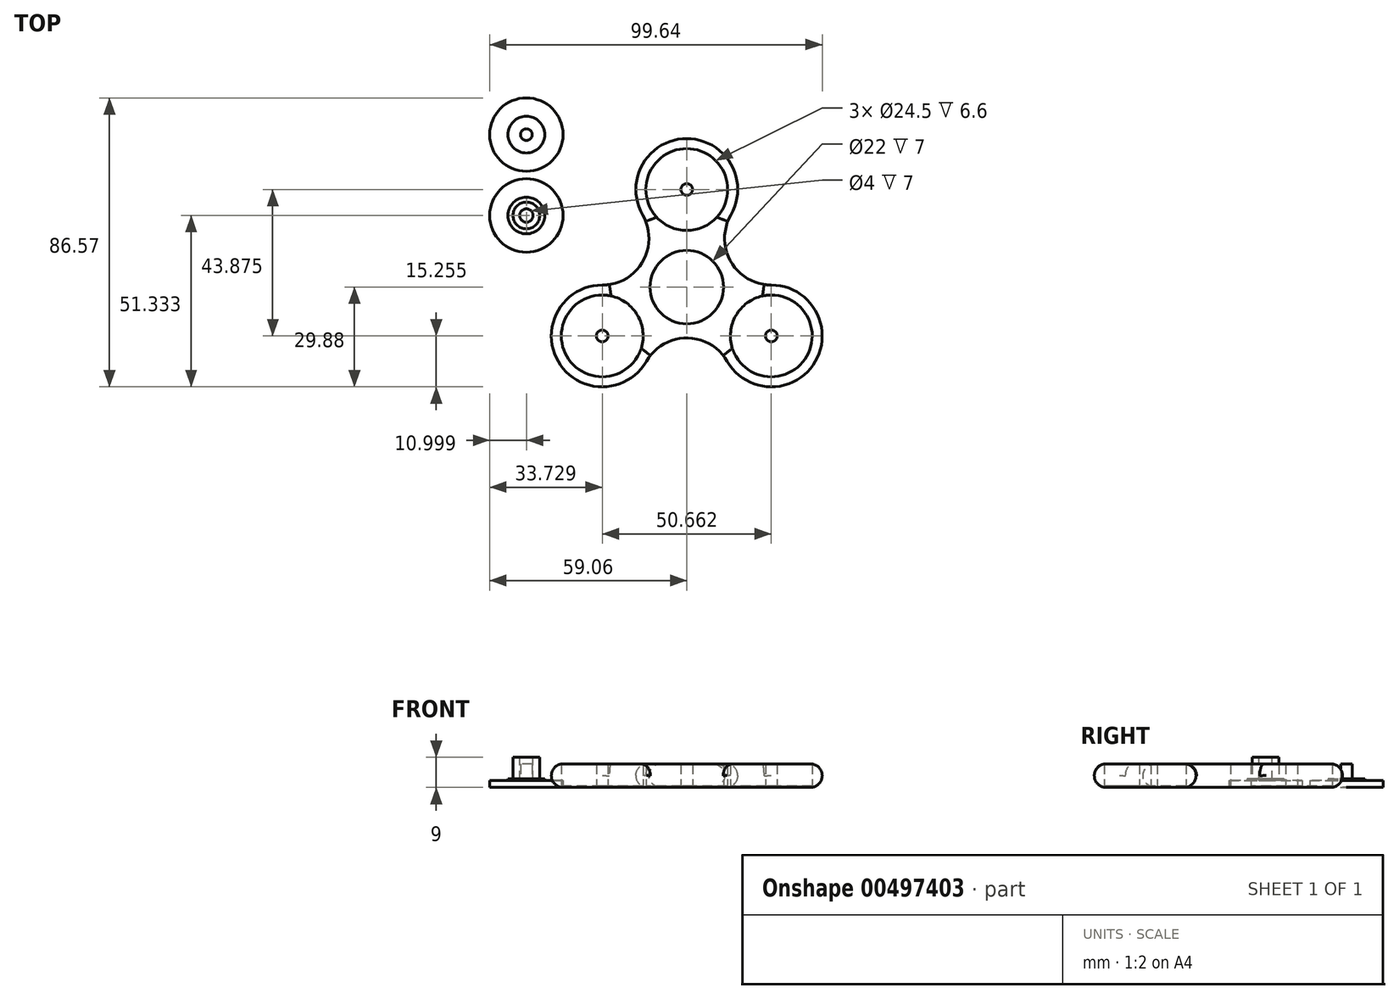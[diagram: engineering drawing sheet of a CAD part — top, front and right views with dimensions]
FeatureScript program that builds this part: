
annotation { "Feature Type Name" : "Feature", "Feature Type Description" : "" }
export const myFeature = defineFeature(function(context is Context, id is Id, definition is map)
    precondition{}
    {
        {
            var Q0;
            Q0=qCreatedBy(makeId("Top.planeOp"),FACE);
            var sketch = newSketch(context, id + "F0", { "sketchPlane" : qUnion([Q0])});
            skCircle(sketch, "E0", {"center": v(0, 0) * mm, "radius": 11 * mm});
            skCircle(sketch, "E1", {"center": v(0, 0) * mm, "radius": 14 * mm});
            skCircle(sketch, "E2", {"center": v(0, 29.25) * mm, "radius": 12.25 * mm});
            skCircle(sketch, "E3", {"center": v(0, 29.25) * mm, "radius": 1.75 * mm});
            skCircle(sketch, "E4", {"center": v(0, 29.25) * mm, "radius": 15.25 * mm});
            skCircle(sketch, "E5.1.0", {"center": v(-25.33, -14.62) * mm, "radius": 15.25 * mm});
            skCircle(sketch, "E5.1.1", {"center": v(-25.33, -14.62) * mm, "radius": 1.75 * mm});
            skCircle(sketch, "E5.1.2", {"center": v(-25.33, -14.62) * mm, "radius": 12.25 * mm});
            skCircle(sketch, "E5.2.0", {"center": v(25.33, -14.62) * mm, "radius": 15.25 * mm});
            skCircle(sketch, "E5.2.1", {"center": v(25.33, -14.62) * mm, "radius": 1.75 * mm});
            skCircle(sketch, "E5.2.2", {"center": v(25.33, -14.62) * mm, "radius": 12.25 * mm});
            skArc(sketch, "E6", {"start": v(-25.33, 0.63) * mm, "mid": v(-13.2, 7.62) * mm, "end": v(-13.2, 21.62) * mm});
            skArc(sketch, "E7.1.0", {"start": v(12.12, -22.25) * mm, "mid": v(0, -15.25) * mm, "end": v(-12.12, -22.25) * mm});
            skArc(sketch, "E7.2.0", {"start": v(13.2, 21.63) * mm, "mid": v(13.2, 7.63) * mm, "end": v(25.33, 0.63) * mm});
            skSolve(sketch);
        }
        {
            var Q0;
            Q0=makeQuery(id+"F0.imprint","IMPRINT",FACE,{"disambiguationData":[TD([[makeQuery(id+"F0.imprint","IMPRINT",EDGE,{"derivedFrom":sQuery(id+"F0.wireOp",EDGE,"E2")}),-1.0]])]});
            var Q1;
            {var subQ5=sQuery(id+"F0.wireOp",EDGE,"E6");Q1=makeQuery(id+"F0.imprint","IMPRINT",FACE,{"disambiguationData":[TD([[makeQuery(id+"F0.imprint","IMPRINT",EDGE,{"derivedFrom":subQ5}),-1.0]])]});}
            var Q2;
            Q2=makeQuery(id+"F0.imprint","IMPRINT",FACE,{"disambiguationData":[TD([[makeQuery(id+"F0.imprint","IMPRINT",EDGE,{"derivedFrom":sQuery(id+"F0.wireOp",EDGE,"E0")}),-1.0]])]});
            var Q3;
            {var subQ5=sQuery(id+"F0.wireOp",EDGE,"E7.2.0");Q3=makeQuery(id+"F0.imprint","IMPRINT",FACE,{"disambiguationData":[TD([[makeQuery(id+"F0.imprint","IMPRINT",EDGE,{"derivedFrom":subQ5}),-1.0]])]});}
            var Q4;
            Q4=makeQuery(id+"F0.imprint","IMPRINT",FACE,{"disambiguationData":[TD([[makeQuery(id+"F0.imprint","IMPRINT",EDGE,{"derivedFrom":sQuery(id+"F0.wireOp",EDGE,"E5.2.2")}),-1.0]])]});
            var Q5;
            {var subQ5=sQuery(id+"F0.wireOp",EDGE,"E7.1.0");Q5=makeQuery(id+"F0.imprint","IMPRINT",FACE,{"disambiguationData":[TD([[makeQuery(id+"F0.imprint","IMPRINT",EDGE,{"derivedFrom":subQ5}),-1.0]])]});}
            var Q6;
            Q6=makeQuery(id+"F0.imprint","IMPRINT",FACE,{"disambiguationData":[TD([[makeQuery(id+"F0.imprint","IMPRINT",EDGE,{"derivedFrom":sQuery(id+"F0.wireOp",EDGE,"E5.1.2")}),-1.0]])]});
            extrude(context, id + "F1", {"entities" : qUnion([Q0, Q1, Q2, Q3, Q4, Q5, Q6]), "depth" : 7 * mm});
        }
        {
            var Q0;
            Q0=makeQuery(id+"F0.imprint","IMPRINT",FACE,{"disambiguationData":[TD([[makeQuery(id+"F0.imprint","IMPRINT",EDGE,{"derivedFrom":sQuery(id+"F0.wireOp",EDGE,"E2")}),1.0]])]});
            var Q1;
            Q1=makeQuery(id+"F0.imprint","IMPRINT",FACE,{"disambiguationData":[TD([[makeQuery(id+"F0.imprint","IMPRINT",EDGE,{"derivedFrom":sQuery(id+"F0.wireOp",EDGE,"E5.1.1")}),-1.0]])]});
            var Q2;
            Q2=makeQuery(id+"F0.imprint","IMPRINT",FACE,{"disambiguationData":[TD([[makeQuery(id+"F0.imprint","IMPRINT",EDGE,{"derivedFrom":sQuery(id+"F0.wireOp",EDGE,"E5.2.1")}),-1.0]])]});
            extrude(context, id + "F2", {"entities" : qUnion([Q0, Q1, Q2]), "operationType" : NewBodyOperationType.ADD, "depth" : 0.4 * mm});
        }
        {
            var Q0;
            Q0=makeQuery(id+"F0.imprint","IMPRINT",FACE,{"disambiguationData":[TD([[makeQuery(id+"F0.imprint","IMPRINT",EDGE,{"derivedFrom":sQuery(id+"F0.wireOp",EDGE,"E3")}),1.0]])]});
            var Q1;
            Q1=makeQuery(id+"F0.imprint","IMPRINT",FACE,{"disambiguationData":[TD([[makeQuery(id+"F0.imprint","IMPRINT",EDGE,{"derivedFrom":sQuery(id+"F0.wireOp",EDGE,"E5.1.1")}),1.0]])]});
            var Q2;
            Q2=makeQuery(id+"F0.imprint","IMPRINT",FACE,{"disambiguationData":[TD([[makeQuery(id+"F0.imprint","IMPRINT",EDGE,{"derivedFrom":sQuery(id+"F0.wireOp",EDGE,"E5.2.1")}),1.0]])]});
            extrude(context, id + "F3", {"entities" : qUnion([Q0, Q1, Q2]), "operationType" : NewBodyOperationType.ADD, "depth" : 7 * mm});
        }
        {
            var Q0;
            Q0=makeQuery(id+"F1.opExtrude","CAP_EDGE",EDGE,{"disambiguationData":[OSD([sQuery(id+"F0.wireOp",EDGE,"E5.1.0")])],"isStart":false});
            var Q1;
            Q1=makeQuery(id+"F1.opExtrude","CAP_EDGE",EDGE,{"disambiguationData":[OSD([sQuery(id+"F0.wireOp",EDGE,"E5.1.0")])],"isStart":true});
            fillet(context, id + "F4", {"entities" : qUnion([Q0, Q1]), "radius" : 3.5 * mm, "tangentPropagation" : true, "allowEdgeOverflow" : false});
        }
        {
            var Q0;
            Q0=qCreatedBy(makeId("Top.planeOp"),FACE);
            var sketch = newSketch(context, id + "F5", { "sketchPlane" : qUnion([Q0])});
            skCircle(sketch, "E8", {"center": v(-48.06, 21.45) * mm, "radius": 11 * mm});
            skCircle(sketch, "E9", {"center": v(-48.06, 45.69) * mm, "radius": 11 * mm});
            skSolve(sketch);
        }
        {
            var Q0;
            Q0=makeQuery(id+"F5.imprint","IMPRINT",FACE,{"disambiguationData":[TD([[makeQuery(id+"F5.imprint","IMPRINT",EDGE,{"derivedFrom":sQuery(id+"F5.wireOp",EDGE,"E8")}),1.0]])]});
            var Q1;
            Q1=makeQuery(id+"F5.imprint","IMPRINT",FACE,{"disambiguationData":[TD([[makeQuery(id+"F5.imprint","IMPRINT",EDGE,{"derivedFrom":sQuery(id+"F5.wireOp",EDGE,"E9")}),1.0]])]});
            extrude(context, id + "F6", {"entities" : qUnion([Q0, Q1]), "depth" : 2 * mm});
        }
        {
            var Q0;
            Q0=makeQuery(id+"F6.opExtrude","CAP_FACE",FACE,{"disambiguationData":[OSD([sQuery(id+"F5.wireOp",EDGE,"E8")])],"isStart":false});
            var sketch = newSketch(context, id + "F7", { "sketchPlane" : qUnion([Q0])});
            skCircle(sketch, "E10", {"center": v(-48.06, 21.45) * mm, "radius": 4 * mm});
            skSolve(sketch);
        }
        {
            var Q0;
            Q0=makeQuery(id+"F7.imprint","IMPRINT",FACE,{"disambiguationData":[TD([[makeQuery(id+"F7.imprint","IMPRINT",EDGE,{"derivedFrom":sQuery(id+"F7.wireOp",EDGE,"E10")}),1.0]])]});
            extrude(context, id + "F8", {"entities" : qUnion([Q0]), "operationType" : NewBodyOperationType.ADD, "depth" : 7 * mm});
        }
        {
            var Q0;
            Q0=makeQuery(id+"F8.opExtrude","CAP_FACE",FACE,{"disambiguationData":[OSD([sQuery(id+"F7.wireOp",EDGE,"E10")])],"isStart":false});
            var sketch = newSketch(context, id + "F9", { "sketchPlane" : qUnion([Q0])});
            skCircle(sketch, "E11", {"center": v(-48.06, 21.45) * mm, "radius": 2 * mm});
            skSolve(sketch);
        }
        {
            var Q0;
            Q0=makeQuery(id+"F9.imprint","IMPRINT",FACE,{"disambiguationData":[TD([[makeQuery(id+"F9.imprint","IMPRINT",EDGE,{"derivedFrom":sQuery(id+"F9.wireOp",EDGE,"E11")}),1.0]])]});
            extrude(context, id + "F10", {"entities" : qUnion([Q0]), "operationType" : NewBodyOperationType.REMOVE, "oppositeDirection" : true, "depth" : 7 * mm});
        }
        {
            var Q0;
            Q0=makeQuery(id+"F6.opExtrude","CAP_FACE",FACE,{"disambiguationData":[OSD([sQuery(id+"F5.wireOp",EDGE,"E9")])],"isStart":false});
            var sketch = newSketch(context, id + "F11", { "sketchPlane" : qUnion([Q0])});
            skCircle(sketch, "E12", {"center": v(-48.06, 45.69) * mm, "radius": 1.75 * mm});
            skSolve(sketch);
        }
        {
            var Q0;
            Q0 = qSketchRegion(id + "F11", true);
            extrude(context, id + "F12", {"entities" : qUnion([Q0]), "operationType" : NewBodyOperationType.ADD, "depth" : 5 * mm});
        }
        {
            var Q0;
            Q0=makeQuery(id+"F6.opExtrude","CAP_FACE",FACE,{"disambiguationData":[OSD([sQuery(id+"F5.wireOp",EDGE,"E8")])],"isStart":false});
            var sketch = newSketch(context, id + "F13", { "sketchPlane" : qUnion([Q0])});
            skCircle(sketch, "E13", {"center": v(-48.06, 21.45) * mm, "radius": 5.5 * mm});
            skCircle(sketch, "E14", {"center": v(-48.06, 45.69) * mm, "radius": 5.5 * mm});
            skSolve(sketch);
        }
        {
            var Q0;
            Q0=makeQuery(id+"F13.imprint","IMPRINT",FACE,{"disambiguationData":[TD([[makeQuery(id+"F13.imprint","IMPRINT",EDGE,{"derivedFrom":sQuery(id+"F13.wireOp",EDGE,"E14")}),1.0]])]});
            var Q1;
            Q1=makeQuery(id+"F13.imprint","IMPRINT",FACE,{"disambiguationData":[TD([[makeQuery(id+"F13.imprint","IMPRINT",EDGE,{"derivedFrom":sQuery(id+"F13.wireOp",EDGE,"E13")}),1.0]])]});
            extrude(context, id + "F14", {"entities" : qUnion([Q0, Q1]), "operationType" : NewBodyOperationType.ADD, "depth" : 0.5 * mm});
        }
    });
